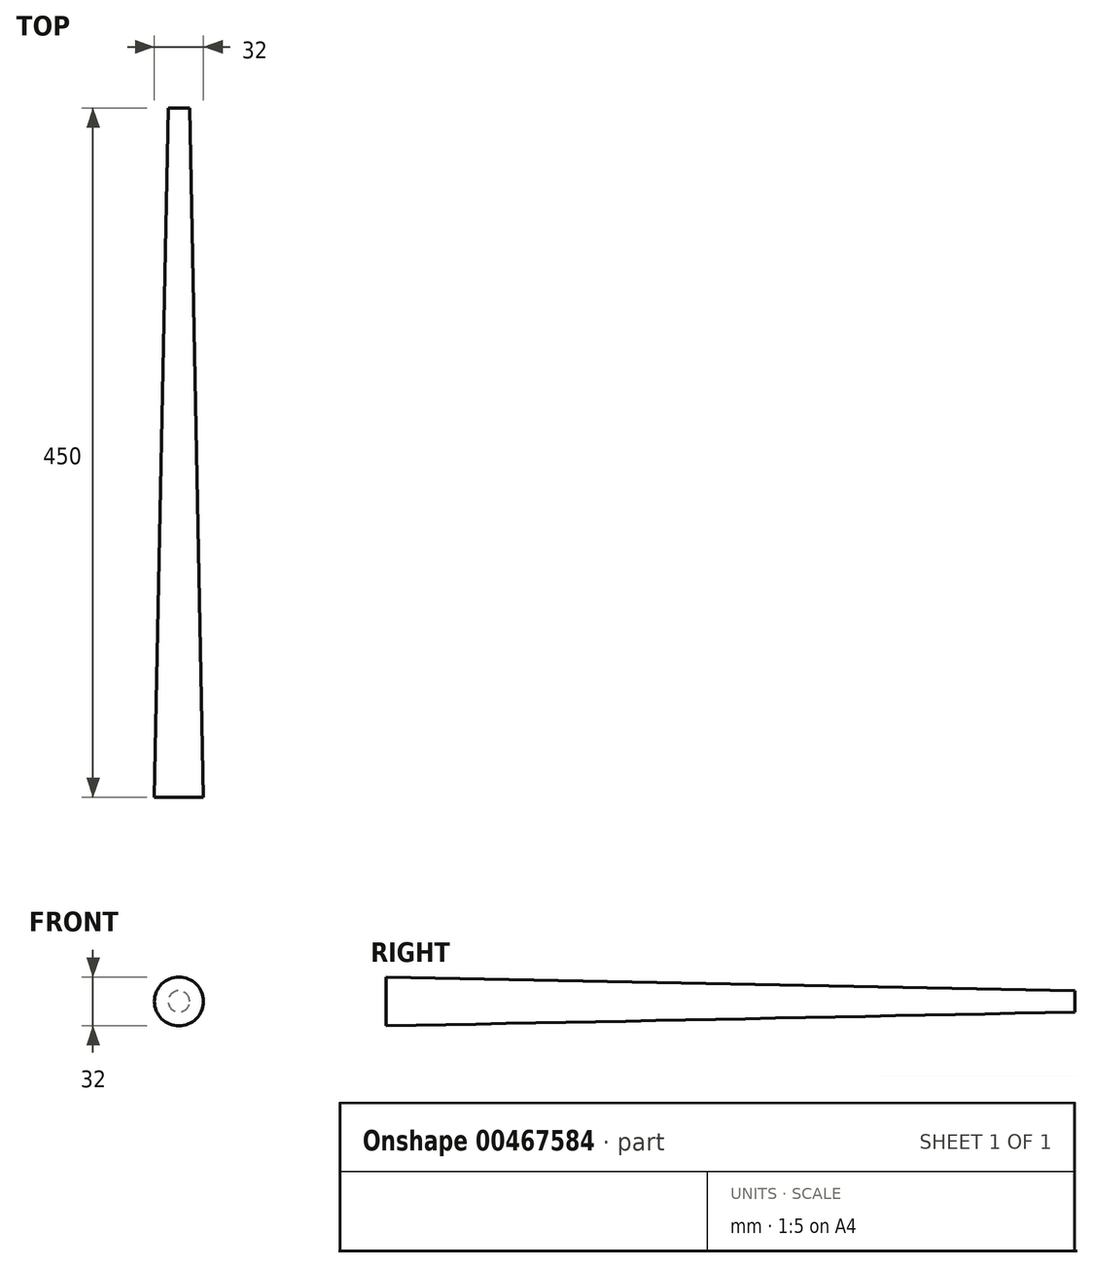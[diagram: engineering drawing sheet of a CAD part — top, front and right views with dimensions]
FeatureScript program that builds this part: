
annotation { "Feature Type Name" : "Feature", "Feature Type Description" : "" }
export const myFeature = defineFeature(function(context is Context, id is Id, definition is map)
    precondition{}
    {
        {
            var Q0;
            Q0=qCreatedBy(makeId("Top.planeOp"),FACE);
            var sketch = newSketch(context, id + "F0", { "sketchPlane" : qUnion([Q0])});
            skLineSegment(sketch, "E0", {"start": v(0, 0) * mm, "end": v(0, 450) * mm});
            skLineSegment(sketch, "E1", {"start": v(0, 0) * mm, "end": v(-16, 0) * mm});
            skLineSegment(sketch, "E2", {"start": v(-16, 0) * mm, "end": v(-7, 450) * mm});
            skLineSegment(sketch, "E3", {"start": v(-7, 450) * mm, "end": v(0, 450) * mm});
            skSolve(sketch);
        }
        {
            var Q0;
            Q0=makeQuery(id+"F0.imprint","IMPRINT",FACE,{"disambiguationData":[TD([[makeQuery(id+"F0.imprint","IMPRINT",EDGE,{"derivedFrom":sQuery(id+"F0.wireOp",EDGE,"E0")}),1.0]])]});
            var Q1;
            Q1=sQuery(id+"F0.wireOp",EDGE,"E0");
            revolve(context, id + "F1", {"entities" : qUnion([Q0]), "axis" : qUnion([Q1]), "revolveType" : RevolveType.FULL});
        }
    });
